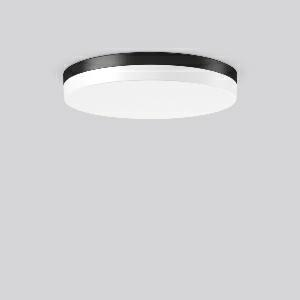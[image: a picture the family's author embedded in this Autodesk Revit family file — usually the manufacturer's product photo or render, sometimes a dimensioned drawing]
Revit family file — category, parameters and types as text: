
# Revit family: flat_slim_round_312634_0031_1_76_26e6
name_source: partatom
category: Lighting Fixtures
units: mm (PartAtom-declared; Revit-internal decimal feet)

## family parameters
Cut with Voids When Loaded = No
Host = Face
Light Source = No
Part Type = Normal
Room Calculation Point = No
Round Connector Dimension = Use Diameter
Shared = No

## types (1)
- MultiLumen 1 830 (1 x LED Modul 830, 3500 lm, 3000)
    Apparent Load = 24 VA
    CIE Flux Codes = 38 68 89 85 100
    Color Rendering = 80
    Color Temperature = 3000
    Default Elevation = 1800 mm
    Height = 70 mm
    Lamp = 1 x LED Modul 830
    Lamp Light Flux = 3500 lm
    Lamp count = 1
    Length = 480 mm
    Lifetime = 50000 h
    Luminous efficacy = 146 lm/W
    Manufacturer = RZB
    ModVariant = No
    Model = 312634.0031.1.76
    Mounting Place = Ceiling
    Mounting Type = Surface mounted
    Number of Poles = 1
    OnlyDefault = Yes
    Power Factor = 1
    Product Name = FLAT SLIM round
    Product group = Surface mounted ceiling and wall luminaires
    ProductGroupID = 305
    Protection Class = Protection class I
    Protection Degree = Degree of protection
    RLX_Detail_Level = 1
    RLX_Emergency_Light_Flux = 0 lm
    RLX_Emergency_Type = 0
    RLX_Emergency_Type_DB = No
    RlxData = <blob elided: 22817 chars, md5=9ab0cfbe>
    Socket = socket
    Standby Power = 0 W
    System Light Flux = 3500 lm
    System Power = 24 W
    Type Comments = MultiLumen 1 830
    Type Image = 312633.0031.jpg
    URL = http://relux.com
    VarID = multilumen_1_830
    Voltage = 0 V
    Weight = 0.00 kg
    Width = 0 mm  [stored 0 ft]

note: [stored X ft] marks values corroborated as IEEE doubles in the binary element streams (Revit-internal decimal feet)

## geometry (parser evidence)
native form markers: Blend x4, Sweep x11
no freeform markers — native parametric forms only
